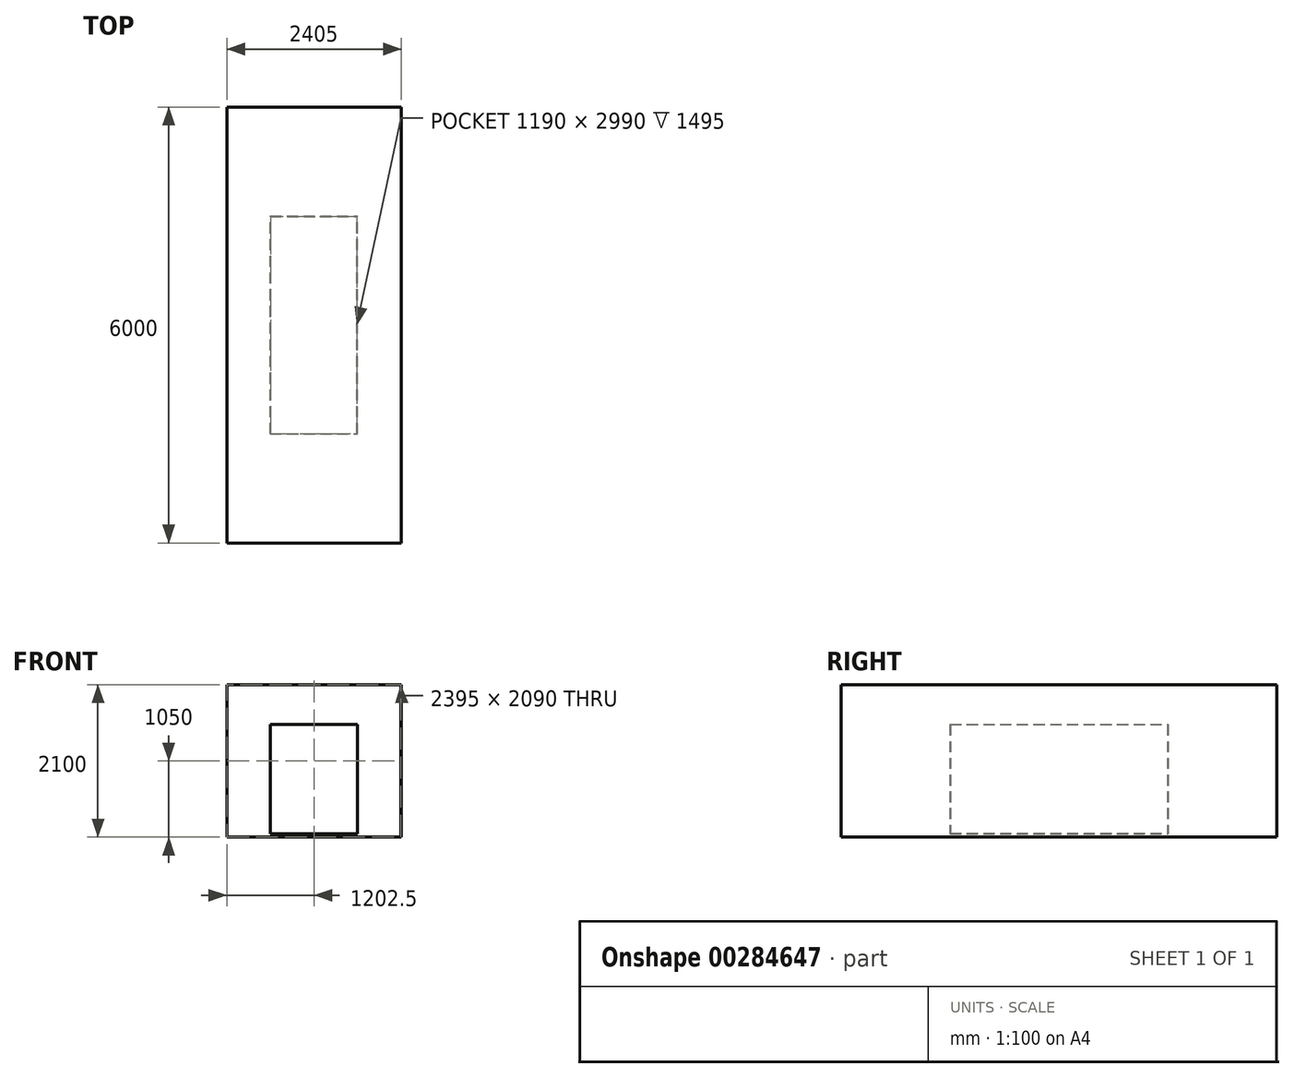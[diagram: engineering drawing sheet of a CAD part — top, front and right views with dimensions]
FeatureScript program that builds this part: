
annotation { "Feature Type Name" : "Feature", "Feature Type Description" : "" }
export const myFeature = defineFeature(function(context is Context, id is Id, definition is map)
    precondition{}
    {
        {
            var Q0;
            Q0=qCreatedBy(makeId("Front.planeOp"),FACE);
            var sketch = newSketch(context, id + "F0", { "sketchPlane" : qUnion([Q0])});
            skLineSegment(sketch, "E0.bottom", {"start": v(-600, 750) * mm, "end": v(600, 750) * mm});
            skLineSegment(sketch, "E0.top", {"start": v(-600, -750) * mm, "end": v(600, -750) * mm});
            skLineSegment(sketch, "E0.left", {"start": v(-600, 750) * mm, "end": v(-600, -750) * mm});
            skLineSegment(sketch, "E0.right", {"start": v(600, 750) * mm, "end": v(600, -750) * mm});
            skPoint(sketch, "E0.middle", {"position": v(0, 0) * mm});
            skSolve(sketch);
        }
        {
            var Q0;
            Q0=makeQuery(id+"F0.imprint","IMPRINT",FACE,{"disambiguationData":[TD([[makeQuery(id+"F0.imprint","IMPRINT",EDGE,{"derivedFrom":sQuery(id+"F0.wireOp",EDGE,"E0.bottom")}),-1.0]])]});
            extrude(context, id + "F1", {"entities" : qUnion([Q0]), "endBound" : BoundingType.SYMMETRIC, "depth" : 3000 * mm});
        }
        {
            var Q0;
            Q0=makeQuery(id+"F1.opExtrude","SWEPT_FACE",FACE,{"disambiguationData":[OSD([sQuery(id+"F0.wireOp",EDGE,"E0.bottom")])]});
            shell(context, id + "F2", {"entities" : qUnion([Q0]), "thickness" : 5 * mm});
        }
        {
            var Q0;
            Q0=qCreatedBy(makeId("Front.planeOp"),FACE);
            var sketch = newSketch(context, id + "F3", { "sketchPlane" : qUnion([Q0])});
            skLineSegment(sketch, "E1.bottom", {"start": v(1200, 1295) * mm, "end": v(-1195, 1295) * mm});
            skLineSegment(sketch, "E1.top", {"start": v(1200, -795) * mm, "end": v(-1195, -795) * mm});
            skLineSegment(sketch, "E1.left", {"start": v(1200, 1295) * mm, "end": v(1200, -795) * mm});
            skLineSegment(sketch, "E1.right", {"start": v(-1195, 1295) * mm, "end": v(-1195, -795) * mm});
            skPoint(sketch, "E1.middle", {"position": v(0, 0) * mm});
            skLineSegment(sketch, "E2.0", {"start": v(1205, 1300) * mm, "end": v(-1200, 1300) * mm});
            skLineSegment(sketch, "E2.1", {"start": v(1205, 1300) * mm, "end": v(1205, -800) * mm});
            skLineSegment(sketch, "E2.2", {"start": v(1205, -800) * mm, "end": v(-1200, -800) * mm});
            skLineSegment(sketch, "E2.3", {"start": v(-1200, 1300) * mm, "end": v(-1200, -800) * mm});
            skSolve(sketch);
        }
        {
            var Q0;
            Q0=makeQuery(id+"F3.imprint","IMPRINT",FACE,{"disambiguationData":[TD([[makeQuery(id+"F3.imprint","IMPRINT",EDGE,{"derivedFrom":sQuery(id+"F3.wireOp",EDGE,"E1.bottom")}),-1.0]])]});
            extrude(context, id + "F4", {"entities" : qUnion([Q0]), "endBound" : BoundingType.SYMMETRIC, "oppositeDirection" : true, "depth" : 6000 * mm});
        }
    });
